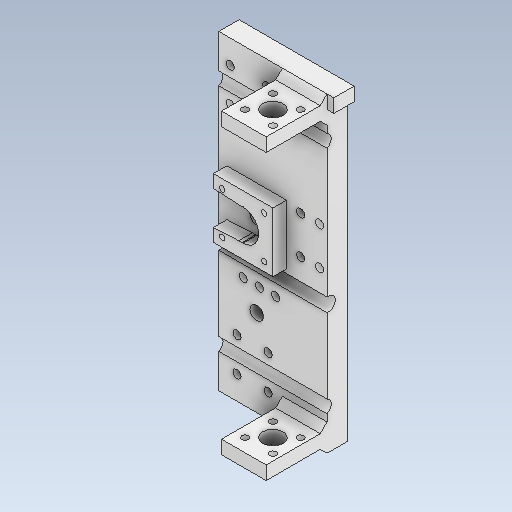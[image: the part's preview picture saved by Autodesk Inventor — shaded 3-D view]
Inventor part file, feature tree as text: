
AUTODESK INVENTOR PART (.ipt)
format: ipt  version: 2020 (Build 240168000, 168)  size: 395,264 bytes
history: native  units: mm
features: reference x18, sketch x15, extrude x13, other x9, chamfer x3, hole x2, projected_geometry x2, fillet x1, mirror x1
ambient origin geometry x8: Origin, YZ Plane, XZ Plane, XY Plane, X Axis, Y Axis, Z Axis, Center Point
bodies: Solid1 (feature_tree)
feature tree (64):
  extrude  "Extrusion1"  Depth=80.0mm
  extrude  "Extrusion2"  Depth=15.0mm
  extrude  "Extrusion3"  Depth=30.0mm
  extrude  "Extrusion4"  Depth=30.0mm
  extrude  "Extrusion5"  Depth=1.0mm
  extrude  "Extrusion6"  Depth=95.0mm
  hole  "Hole1"  [1 undecoded]
  extrude  "Extrusion7"  Depth=25.0mm
  extrude  "Extrusion8"  Depth=10.0mm
  chamfer  "Chamfer1"  [1 undecoded]
  chamfer  "Chamfer2"  Distance=10.0mm
  fillet  "Fillet3"  Radius=23.0mm
  extrude  "Extrusion9"  Depth=10.0mm
  extrude  "Extrusion10"  Depth=105.0mm
  extrude  "Extrusion11"  Depth=105.0mm
  mirror  "Mirror3"
  chamfer  "Chamfer4"  Distance=44.0mm
  extrude  "Extrusion12"  Depth=10.0mm TaperAngle=45.0deg
  hole  "Hole2"  [1 undecoded]
  extrude  "Extrusion13"  Depth=50.0mm
  sketch  "Sketch1"  dims[d0=230.0mm d1=80.0mm]
  sketch  "Sketch2"  dims[d2=15.0mm d3=0.0mm d4=10.3mm]
  sketch  "Sketch3"  dims[d5=2.0mm d6=30.0mm]
  sketch  "Sketch5"  dims[d7=2.0mm d8=30.0mm]
  sketch  "Sketch6"  dims[d9=0.0mm d10=0.0mm d11=1.0mm]
  sketch  "Sketch7"  dims[d12=10.3mm d13=95.0mm]
  sketch  "Sketch8"  dims[d14=25.0mm d15=0.0mm d17=44.0mm]
  sketch  "Sketch9"  dims[d18=10.0mm d19=0.0mm d20=25.0mm]
  projected_geometry  "Projected Loop1"
  sketch  "Sketch10"  dims[d21=3.0mm d22=0.0mm d23=10.0mm d24=0.0mm d25=0.0mm]
  sketch  "Sketch11"  dims[d26=31.0mm]
  reference  "Reference4"
  sketch  "Sketch13"  dims[d27=4.0mm d28=6.0mm d29=7.0mm d30=3.0mm d31=90.0deg d32=8.0mm d33=20.594885mm d35=10.0mm d36=0.0mm d38=23.0mm]
  sketch  "Sketch14"  dims[d39=10.0mm d40=0.0mm d43=105.0mm]
  projected_geometry  "Projected Loop2"
  sketch  "Sketch16"  dims[d45=105.0mm d47=105.0mm]
  sketch  "Sketch17"  dims[d49=105.0mm d52=105.0mm]
  reference  "Reference14"
  reference  "Reference15"
  reference  "Reference16"
  reference  "Reference17"
  reference  "Reference18"
  reference  "Reference19"
  reference  "Reference20"
  reference  "Reference21"
  reference  "Reference22"
  reference  "Reference23"
  reference  "Reference24"
  sketch  "Sketch18"  dims[d54=105.0mm d55=44.0mm d56=1.0mm d57=20.0mm d58=45.0deg d59=1.0mm d60=20.0mm d61=45.0deg d62=50.0mm d64=52.0mm d65=52.0mm d66=52.0mm d67=52.0mm d68=52.0mm d69=44.0mm d70=52.0mm d71=10.0mm d72=5.0mm d73=33.0mm d74=45.0mm d75=0.0mm d81=4.746952mm d82=9.746952mm d83=5.0mm d84=20.506097mm d85=20.506097mm d86=0.0mm d87=0.0mm d88=15.0mm d89=20.0mm d90=15.0mm d94=9.0mm d95=35.0mm d96=0.0mm d97=5.0mm d98=2.0mm d99=45.0deg d101=5.0mm d102=10.0mm d103=0.0mm d104=6.0mm d105=6.0mm d106=4.0mm d107=2.0mm d108=90.0deg d109=8.0mm d110=20.594885mm d111=10.0mm d112=61.174587mm d113=0.0mm d114=0.0mm]
  reference  "Reference25"
  reference  "Reference26"
  reference  "Reference27"
  reference  "Reference28"
  reference  "Reference29"
  reference  "Reference30"
  other  "<path> 2.1 Aracet.iam"
  other  "I.A.B 2.1 Aracet.iam"
  other  "0008-10-1013 LMK 10 Bearing.ipt:22"
  other  "0008-10-010 Fixare AxaX.ipt:23"
  other  "0008-10-011 Fixare AxaX Mijloc.ipt:53"
  other  "0008-10-010 Fixare AxaX:4"
  other  "0008-10-010 Fixare AxaX:2"
  other  "0008-10-1011 GT2 Timing Pulley 20 Tooth.ipt:16"
  other  "0008-10-013 Supăort Piulita Axa Z.ipt:33"
note: 3 required parameter values undecoded (feature->parameter linkage not recoverable at this tier; creation-order binding heuristic only, values carry confidence <= 0.55)
note: 1 file-system path scrubbed to <path> (originals preserved in map.json)
